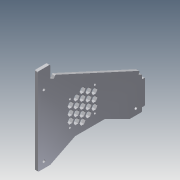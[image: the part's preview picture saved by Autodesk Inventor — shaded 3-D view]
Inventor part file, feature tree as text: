
AUTODESK INVENTOR PART (.ipt)
format: ipt  version: 2014 (Build 180170000, 170)  size: 614,400 bytes
history: native  units: mm
features: extrude x8, sketch x7, fillet x1, pattern_linear x1, projected_geometry x1
ambient origin geometry x8: Origin, YZ Plane, XZ Plane, XY Plane, X Axis, Y Axis, Z Axis, Center Point
bodies: Solid1 (feature_tree)
feature tree (18):
  extrude  "Extrusion1"  Depth=25.0mm
  extrude  "Extrusion2"  Depth=210.0mm
  extrude  "Extrusion3"  Depth=25.0mm
  extrude  "Extrusion4"  Depth=25.0mm
  extrude  "Extrusion5"  Depth=8.1mm TaperAngle=0.0deg
  fillet  "Fillet1"  Radius=8.1mm
  sketch  "Sketch7"  dims[d11=25.0mm d12=3.0mm d13=0.0mm d14=8.1mm]
  extrude  "Extrusion7"  Depth=6.0mm
  pattern_linear  "Rectangular Pattern1"  Spacing1=12.5mm  [1 undecoded]
  extrude  "Extrusion9"  Depth=6.0mm
  extrude  "Extrusion10"  Depth=6.0mm
  sketch  "Sketch2"  dims[d0=175.0mm d1=25.0mm]
  sketch  "Sketch3"  dims[d3=65.0mm d4=210.0mm]
  sketch  "Sketch4"  dims[d5=6.0mm d6=0.0mm d8=25.0mm]
  sketch  "Sketch6"  dims[d9=25.0mm d10=50.0mm]
  sketch  "Sketch8"  dims[d15=8.1mm d16=6.0mm]
  sketch  "Sketch9"  dims[d17=6.0mm d18=0.0mm d19=12.5mm d20=37.5mm d21=12.5mm d22=12.5mm d23=5.4mm d24=6.0mm d25=0.0mm d26=2.0mm d27=185.0mm d28=85.0mm d33=8.1mm d34=6.0mm d35=0.0mm d36=8.1mm d38=6.0mm d39=50.0mm d41=60.0mm d42=15.0mm d43=60.0mm d44=4.3mm d48=3.5mm d49=12.0mm d50=6.928203mm d51=72.712mm d52=66.0mm d53=10.0mm d54=0.0mm d55=40.0mm d57=24.0mm d58=50.0mm d60=13.856mm d63=6.0mm d64=0.0mm d65=6.0mm d66=0.0mm]
  projected_geometry  "Projected Loop1"
note: 1 required parameter value undecoded (feature->parameter linkage not recoverable at this tier; creation-order binding heuristic only, values carry confidence <= 0.55)
